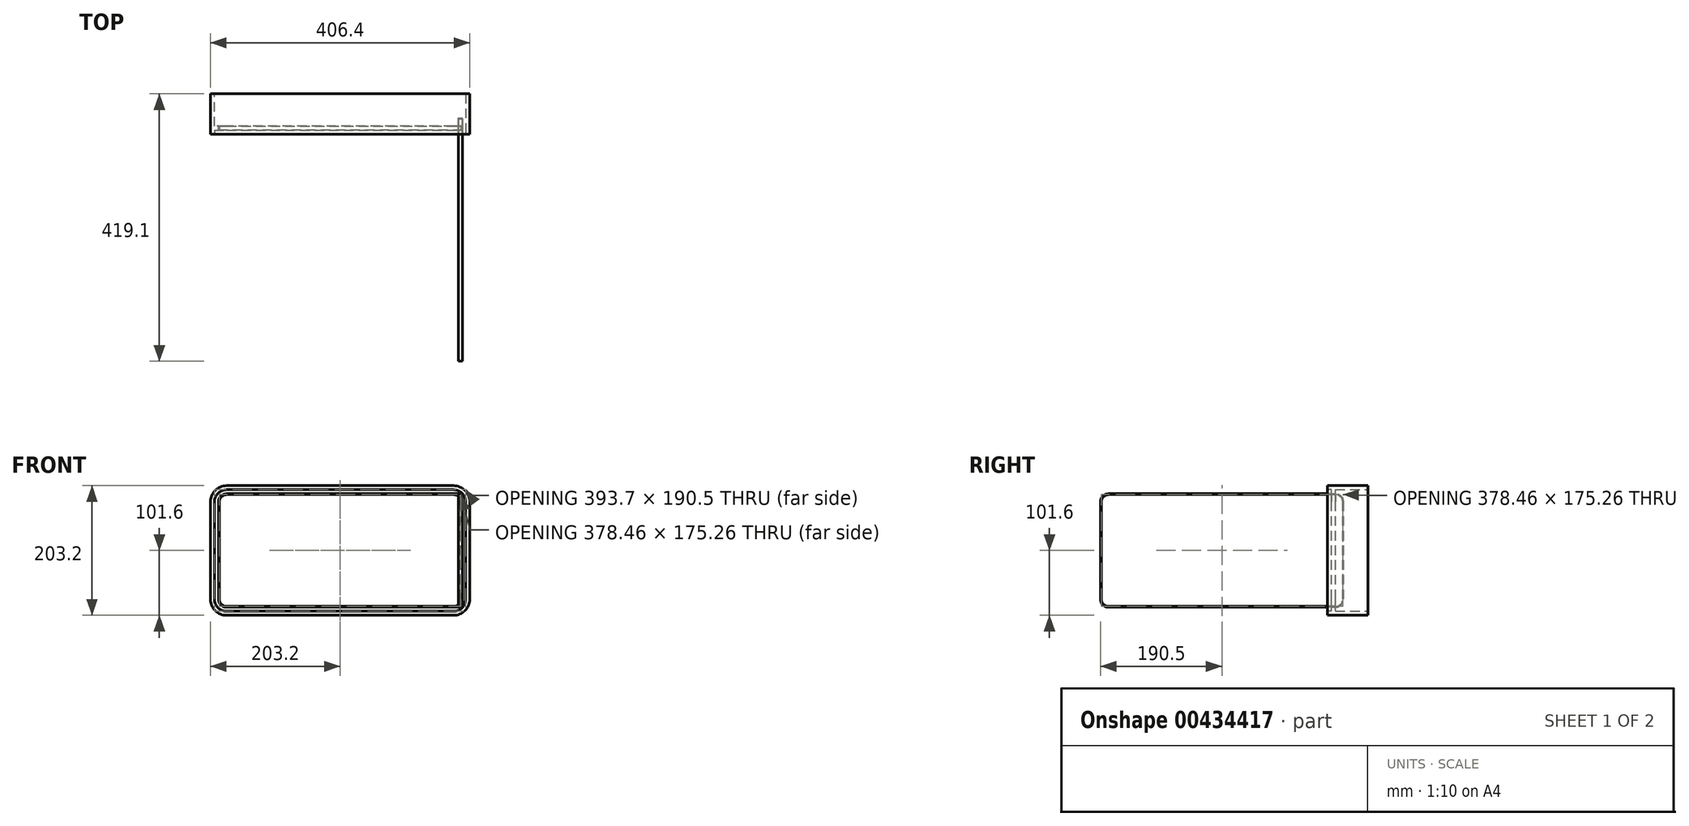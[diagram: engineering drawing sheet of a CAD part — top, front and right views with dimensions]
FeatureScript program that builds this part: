
annotation { "Feature Type Name" : "Feature", "Feature Type Description" : "" }
export const myFeature = defineFeature(function(context is Context, id is Id, definition is map)
    precondition{}
    {
        {
            var Q0;
            Q0=qCreatedBy(makeId("Right.planeOp"),FACE);
            var sketch = newSketch(context, id + "F0", { "sketchPlane" : qUnion([Q0])});
            skLineSegment(sketch, "E0", {"start": v(0, -101.6) * mm, "end": v(0, -95.25) * mm});
            skLineSegment(sketch, "E1", {"start": v(6.35, -88.9) * mm, "end": v(12.7, -88.9) * mm});
            skLineSegment(sketch, "E2", {"start": v(12.7, -88.9) * mm, "end": v(12.7, -95.25) * mm});
            skLineSegment(sketch, "E3", {"start": v(12.7, -95.25) * mm, "end": v(63.5, -95.25) * mm});
            skLineSegment(sketch, "E4", {"start": v(63.5, -95.25) * mm, "end": v(63.5, -101.6) * mm});
            skLineSegment(sketch, "E5", {"start": v(63.5, -101.6) * mm, "end": v(0, -101.6) * mm});
            skLineSegment(sketch, "E6", {"start": v(6.35, -88.9) * mm, "end": v(6.35, -95.25) * mm});
            skLineSegment(sketch, "E7", {"start": v(6.35, -95.25) * mm, "end": v(0, -95.25) * mm});
            skSolve(sketch);
        }
        {
            var Q0;
            Q0=qCreatedBy(makeId("Front.planeOp"),FACE);
            var sketch = newSketch(context, id + "F1", { "sketchPlane" : qUnion([Q0])});
            skLineSegment(sketch, "E8.bottom", {"start": v(0, 101.6) * mm, "end": v(-177.8, 101.6) * mm});
            skLineSegment(sketch, "E8.top", {"start": v(0, -101.6) * mm, "end": v(-177.8, -101.6) * mm});
            skLineSegment(sketch, "E8.right", {"start": v(-203.2, 76.2) * mm, "end": v(-203.2, -76.2) * mm});
            skPoint(sketch, "E8.middle", {"position": v(0, 0) * mm});
            skPoint(sketch, "E9.visualSharp", {"position": v(-203.2, 101.6) * mm});
            skArc(sketch, "E9.filletArc", {"start": v(-177.8, 101.6) * mm, "mid": v(-195.76, 94.16) * mm, "end": v(-203.2, 76.2) * mm});
            skPoint(sketch, "E10.visualSharp", {"position": v(-203.2, -101.6) * mm});
            skArc(sketch, "E10.filletArc", {"start": v(-203.2, -76.2) * mm, "mid": v(-195.76, -94.16) * mm, "end": v(-177.8, -101.6) * mm});
            skPoint(sketch, "E11.visualSharp", {"position": v(203.2, 101.6) * mm});
            skPoint(sketch, "E12.visualSharp", {"position": v(203.2, -101.6) * mm});
            skPoint(sketch, "E13", {"position": v(0, 101.6) * mm});
            skPoint(sketch, "E14", {"position": v(0, -101.6) * mm});
            skPoint(sketch, "E11.filletArc.end.orphan", {"position": v(177.8, 101.6) * mm});
            skPoint(sketch, "E15.orphan", {"position": v(177.8, -101.6) * mm});
            skSolve(sketch);
        }
        {
            var Q0;
            Q0=makeQuery(id+"F0.imprint","IMPRINT",FACE,{"disambiguationData":[TD([[makeQuery(id+"F0.imprint","IMPRINT",EDGE,{"derivedFrom":sQuery(id+"F0.wireOp",EDGE,"E0")}),-1.0]])]});
            var Q1;
            Q1=qConstructionFilter(qBodyType(qCreatedBy(id+"F1",EDGE),BodyType.WIRE),ConstructionObject.NO);
            sweep(context, id + "F2", {"profiles" : qUnion([Q0]), "path" : qUnion([Q1])});
        }
        {
            var Q0;
            Q0=makeQuery(id+"F2.opSweep","SWEPT_BODY",BODY,{"disambiguationData":[OSD([sQuery(id+"F0.wireOp",EDGE,"E0"),sQuery(id+"F0.wireOp",EDGE,"dsh9ijw1-W129-J2vh-FH4a-NIyJqDmt8xat"),sQuery(id+"F0.wireOp",EDGE,"E1"),sQuery(id+"F0.wireOp",EDGE,"E2"),sQuery(id+"F0.wireOp",EDGE,"E3"),sQuery(id+"F0.wireOp",EDGE,"E4"),sQuery(id+"F0.wireOp",EDGE,"E5"),sQuery(id+"F1.wireOp",EDGE,"E8.top")])]});
            var Q1;
            Q1=qCreatedBy(makeId("Right.planeOp"),FACE);
            mirror(context, id + "F3", {"operationType" : NewBodyOperationType.ADD, "entities" : qUnion([Q0]), "mirrorPlane" : qUnion([Q1])});
        }
        {
            var Q0;
            {var subQ0=makeQuery(id+"F2.opSweep","SWEPT_FACE",FACE,{"disambiguationData":[OSD([sQuery(id+"F0.wireOp",EDGE,"E6"),sQuery(id+"F1.wireOp",EDGE,"E8.top")])]});Q0=makeQuery(id+"F3.boolean.opBoolean","MERGE",FACE,{"derivedFrom":[subQ0,makeQuery(id+"F3.opPattern","COPY",FACE,{"derivedFrom":subQ0,"instanceName":"1"})]});}
            var sketch = newSketch(context, id + "F4", { "sketchPlane" : qUnion([Q0])});
            skLineSegment(sketch, "E16.0", {"start": v(-195.58, -76.2) * mm, "end": v(-195.58, 76.2) * mm});
            skArc(sketch, "E16.1", {"start": v(-177.8, -93.98) * mm, "mid": v(-190.37, -88.77) * mm, "end": v(-195.58, -76.2) * mm});
            skArc(sketch, "E16.2", {"start": v(-195.58, 76.2) * mm, "mid": v(-190.37, 88.77) * mm, "end": v(-177.8, 93.98) * mm});
            skLineSegment(sketch, "E16.3", {"start": v(177.8, -93.98) * mm, "end": v(-177.8, -93.98) * mm});
            skLineSegment(sketch, "E16.4", {"start": v(-177.8, 93.98) * mm, "end": v(177.8, 93.98) * mm});
            skArc(sketch, "E16.5", {"start": v(195.58, 76.2) * mm, "mid": v(190.37, 88.77) * mm, "end": v(177.8, 93.98) * mm});
            skLineSegment(sketch, "E16.6", {"start": v(195.58, -76.2) * mm, "end": v(195.58, 76.2) * mm});
            skArc(sketch, "E16.7", {"start": v(177.8, -93.98) * mm, "mid": v(190.37, -88.77) * mm, "end": v(195.58, -76.2) * mm});
            skArc(sketch, "E17.0", {"start": v(-189.23, 76.2) * mm, "mid": v(-185.88, 84.28) * mm, "end": v(-177.8, 87.63) * mm});
            skLineSegment(sketch, "E17.1", {"start": v(-189.23, -76.2) * mm, "end": v(-189.23, 76.2) * mm});
            skLineSegment(sketch, "E17.2", {"start": v(-177.8, 87.63) * mm, "end": v(177.8, 87.63) * mm});
            skArc(sketch, "E17.3", {"start": v(-177.8, -87.63) * mm, "mid": v(-185.88, -84.28) * mm, "end": v(-189.23, -76.2) * mm});
            skArc(sketch, "E17.4", {"start": v(189.23, 76.2) * mm, "mid": v(185.88, 84.28) * mm, "end": v(177.8, 87.63) * mm});
            skLineSegment(sketch, "E17.5", {"start": v(189.23, -76.2) * mm, "end": v(189.23, 76.2) * mm});
            skArc(sketch, "E17.6", {"start": v(177.8, -87.63) * mm, "mid": v(185.88, -84.28) * mm, "end": v(189.23, -76.2) * mm});
            skLineSegment(sketch, "E17.7", {"start": v(177.8, -87.63) * mm, "end": v(-177.8, -87.63) * mm});
            skSolve(sketch);
        }
        {
            var Q0;
            Q0=makeQuery(id+"F4.imprint","IMPRINT",FACE,{"disambiguationData":[TD([[makeQuery(id+"F4.imprint","IMPRINT",EDGE,{"derivedFrom":sQuery(id+"F4.wireOp",EDGE,"E17.0")}),-1.0]])]});
            extrude(context, id + "F5", {"entities" : qUnion([Q0]), "oppositeDirection" : true, "depth" : 6.35 * mm});
        }
        {
            var Q0;
            Q0=makeQuery(id+"F5.opExtrude","CAP_FACE",FACE,{"disambiguationData":[OSD([sQuery(id+"F4.wireOp",EDGE,"E16.0"),sQuery(id+"F4.wireOp",EDGE,"E16.1"),sQuery(id+"F4.wireOp",EDGE,"E16.2"),sQuery(id+"F4.wireOp",EDGE,"E16.3"),sQuery(id+"F4.wireOp",EDGE,"E16.4"),sQuery(id+"F4.wireOp",EDGE,"E16.5"),sQuery(id+"F4.wireOp",EDGE,"E16.6"),sQuery(id+"F4.wireOp",EDGE,"E16.7")])],"isStart":true});
            var Q1;
            Q1=makeQuery(id+"F5.opExtrude","CAP_FACE",FACE,{"disambiguationData":[OSD([sQuery(id+"F4.wireOp",EDGE,"E17.0"),sQuery(id+"F4.wireOp",EDGE,"E17.1"),sQuery(id+"F4.wireOp",EDGE,"E17.2"),sQuery(id+"F4.wireOp",EDGE,"E17.3"),sQuery(id+"F4.wireOp",EDGE,"E17.4"),sQuery(id+"F4.wireOp",EDGE,"E17.5"),sQuery(id+"F4.wireOp",EDGE,"E17.6"),sQuery(id+"F4.wireOp",EDGE,"E17.7")])],"isStart":false});
            cPlane(context, id + "F6", {"entities" : qUnion([Q0, Q1]), "cplaneType" : CPlaneType.OFFSET, "offset" : 3.8 * mm, "width" : 152.4 * mm, "height" : 152.4 * mm});
        }
        {
            var Q0;
            Q0=qCreatedBy(id+"F6.planeOp",FACE);
            var sketch = newSketch(context, id + "F7", { "sketchPlane" : qUnion([Q0])});
            skLineSegment(sketch, "E18", {"start": v(-181.61, 520.96) * mm, "end": v(-181.6, -518.36) * mm, "construction": true});
            skSolve(sketch);
        }
        {
            var Q0;
            {var subQ0=makeQuery(id+"F2.opSweep","SWEPT_FACE",FACE,{"disambiguationData":[OSD([sQuery(id+"F0.wireOp",EDGE,"E2"),sQuery(id+"F1.wireOp",EDGE,"E8.top")])]});Q0=makeQuery(id+"F3.boolean.opBoolean","MERGE",FACE,{"derivedFrom":[subQ0,makeQuery(id+"F3.opPattern","COPY",FACE,{"derivedFrom":subQ0,"instanceName":"1"})]});}
            var sketch = newSketch(context, id + "F8", { "sketchPlane" : qUnion([Q0])});
            skLineSegment(sketch, "E19.0", {"start": v(-196.85, -76.2) * mm, "end": v(-196.85, 76.2) * mm});
            skArc(sketch, "E19.1", {"start": v(-196.85, 76.2) * mm, "mid": v(-191.27, 89.67) * mm, "end": v(-177.8, 95.25) * mm});
            skLineSegment(sketch, "E19.2", {"start": v(177.8, 95.25) * mm, "end": v(-177.8, 95.25) * mm});
            skLineSegment(sketch, "E19.3", {"start": v(177.8, 88.9) * mm, "end": v(-177.8, 88.9) * mm});
            skArc(sketch, "E19.4", {"start": v(-190.5, 76.2) * mm, "mid": v(-186.78, 85.18) * mm, "end": v(-177.8, 88.9) * mm});
            skLineSegment(sketch, "E19.5", {"start": v(-190.5, -76.2) * mm, "end": v(-190.5, 76.2) * mm});
            skArc(sketch, "E19.6", {"start": v(-177.8, -88.9) * mm, "mid": v(-186.78, -85.18) * mm, "end": v(-190.5, -76.2) * mm});
            skArc(sketch, "E19.7", {"start": v(-177.8, -95.25) * mm, "mid": v(-191.27, -89.67) * mm, "end": v(-196.85, -76.2) * mm});
            skLineSegment(sketch, "E19.8", {"start": v(-177.8, -88.9) * mm, "end": v(177.8, -88.9) * mm});
            skLineSegment(sketch, "E19.9", {"start": v(-177.8, -95.25) * mm, "end": v(177.8, -95.25) * mm});
            skLineSegment(sketch, "E20", {"start": v(-177.8, 95.25) * mm, "end": v(-177.8, -95.25) * mm});
            skLineSegment(sketch, "E21", {"start": v(-177.8, 88.9) * mm, "end": v(-192, 88.9) * mm});
            skLineSegment(sketch, "E22", {"start": v(-177.8, -88.9) * mm, "end": v(-192, -88.9) * mm});
            skSolve(sketch);
        }
        {
            var Q0;
            Q0=makeQuery(id+"F8.imprint","IMPRINT",FACE,{"disambiguationData":[TD([[makeQuery(id+"F8.imprint","IMPRINT",EDGE,{"derivedFrom":sQuery(id+"F8.wireOp",EDGE,"E19.0")}),-1.0]])]});
            var Q1;
            {var subQ0=makeQuery(id+"F2.opSweep","SWEPT_FACE",FACE,{"disambiguationData":[OSD([sQuery(id+"F0.wireOp",EDGE,"E6"),sQuery(id+"F1.wireOp",EDGE,"E8.top")])]});Q1=makeQuery(id+"F3.boolean.opBoolean","MERGE",FACE,{"derivedFrom":[subQ0,makeQuery(id+"F3.opPattern","COPY",FACE,{"derivedFrom":subQ0,"instanceName":"1"})]});}
            extrude(context, id + "F9", {"entities" : qUnion([Q0]), "operationType" : NewBodyOperationType.REMOVE, "endBound" : BoundingType.UP_TO_SURFACE, "oppositeDirection" : true, "endBoundEntityFace" : qUnion([Q1]), "depth" : 25.4 * mm});
        }
        {
            var Q0;
            Q0=makeQuery(id+"F5.opExtrude","SWEPT_BODY",BODY,{"disambiguationData":[OSD([sQuery(id+"F4.wireOp",EDGE,"E17.0"),sQuery(id+"F4.wireOp",EDGE,"E17.1"),sQuery(id+"F4.wireOp",EDGE,"E17.2"),sQuery(id+"F4.wireOp",EDGE,"E17.3"),sQuery(id+"F4.wireOp",EDGE,"E17.4"),sQuery(id+"F4.wireOp",EDGE,"E17.5"),sQuery(id+"F4.wireOp",EDGE,"E17.6"),sQuery(id+"F4.wireOp",EDGE,"E17.7")])]});
            var Q1;
            Q1=sQuery(id+"F7.wireOp",EDGE,"E18");
            transform(context, id + "F10", {"entities" : qUnion([Q0]), "transformType" : TransformType.ROTATION, "transformAxis" : qUnion([Q1]), "angle" : 90 * degree, "oppositeDirection" : true, "makeCopy" : true});
        }
    });
